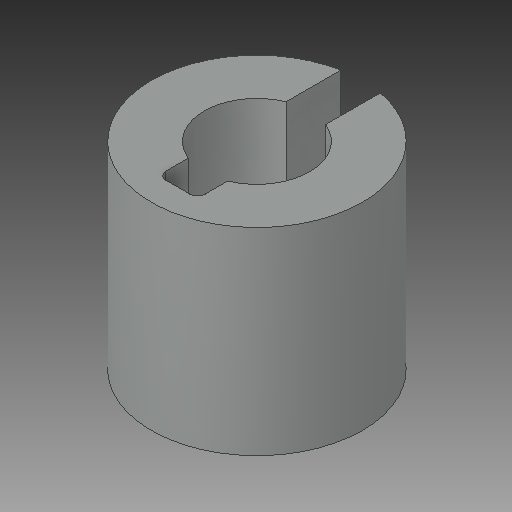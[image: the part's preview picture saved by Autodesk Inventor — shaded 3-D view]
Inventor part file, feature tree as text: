
AUTODESK INVENTOR PART (.ipt)
format: ipt  version: 2017 (Build 210142000, 142)  size: 99,840 bytes
history: native  units: in
note: dims shown in document units (in); Inventor stores cm internally (conversion verified against a paired STEP export)
features: fillet x1
ambient origin geometry x8: Origin, YZ Plane, XZ Plane, XY Plane, X Axis, Y Axis, Z Axis, Center Point
bodies: Solid1 (feature_tree)
feature tree (1):
  fillet  "Fillet1"  [1 undecoded]
note: 1 required parameter value undecoded (feature->parameter linkage not recoverable at this tier; creation-order binding heuristic only, values carry confidence <= 0.55)
